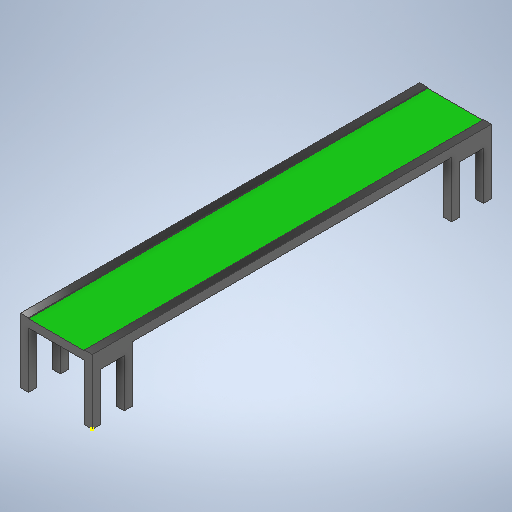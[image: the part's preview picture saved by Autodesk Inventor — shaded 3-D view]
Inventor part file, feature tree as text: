
AUTODESK INVENTOR PART (.ipt)
format: ipt  version: 2025.2 (Build 292293000, 293)  size: 351,232 bytes
history: native  units: mm
features: sketch x6, extrude x5, projected_geometry x1
ambient origin geometry x8: Origin, YZ Plane, XZ Plane, XY Plane, X Axis, Y Axis, Z Axis, Center Point
bodies: Body1 (feature_tree)
feature tree (12):
  extrude  "Extrusion6"  Depth=100.0mm
  extrude  "Extrusion7"  Depth=100.0mm TaperAngle=0.0deg
  sketch  "Sketch11"  dims[d83=500.0mm d84=500.0mm]
  extrude  "Extrusion8"  Depth=500.0mm
  extrude  "Extrusion9"  Depth=600.0mm
  extrude  "Extrusion10"  Depth=500.0mm
  sketch  "Sketch9"  dims[d70=900.0mm d71=100.0mm]
  sketch  "Sketch10"  dims[d72=100.0mm d75=1100.0mm d76=0.0mm]
  sketch  "Sketch12"  dims[d85=600.0mm d86=600.0mm]
  sketch  "Sketch13"  dims[d87=900.0mm d88=0.0mm d89=500.0mm]
  sketch  "Sketch14"  dims[d91=600.0mm d92=500.0mm d93=600.0mm d94=900.0mm d95=0.0mm d96=290.0mm d97=0.0mm d98=100.0mm d99=100.0mm d100=100.0mm d101=100.0mm d102=0.0mm d103=0.0mm d53=0.5mm d54=0.872665mm d55=0.5mm d56=0.872665mm d104=0.5mm d105=0.872665mm]
  projected_geometry  "Projected Loop1"
